# Revit family: Bathtub_Contemporary_FBY1550P_TOTO
name_source: partatom
category: Plumbing Fixtures
revit_build: Autodesk Revit Architecture 2013 (Build: 20130531_2115(x64)
units: mm (PartAtom-declared; Revit-internal decimal feet)

## types (1)
- FBY1550P
    04 CSI = 22 41 19
    95 CSI = 15410
    ADA Compliant = Yes
    Assembly Code = D2010510
    CAD Drawing URL = http://assets.totousa.com
    Color Availability = #01  Cotton, #12  Sedona Beige
    Default Elevation = 48"
    Depth = 59 1/16"
    Description = Enameled Cast Iron Bathtub
    Finish = Metal - TOTO - Chrome - Polished
    Height = 23 1/4"
    Manufacturer = TOTO USA, Inc.
    Manufacturer Fax = (770) 282-0002
    Model = FBY1550P
    Shipping Weight = 346.00 lb
    Spec Sheet URL = http://assets.totousa.com
    Style = Contemporary
    Subcategory = Bathtubs
    Toto BIM Number = BM-00067
    URL = http://www.totousa.com
    Warranty = Lifetime Limited Warranty
    Warranty URL = http://www.totousa.com
    Waste Connection NPT = 2 1/4"
    Water Connection Radius = 1 1/8"
    Width = 31 1/2"

## geometry (parser evidence)
native form markers: Blend x2, Sweep x3
no freeform markers — native parametric forms only
